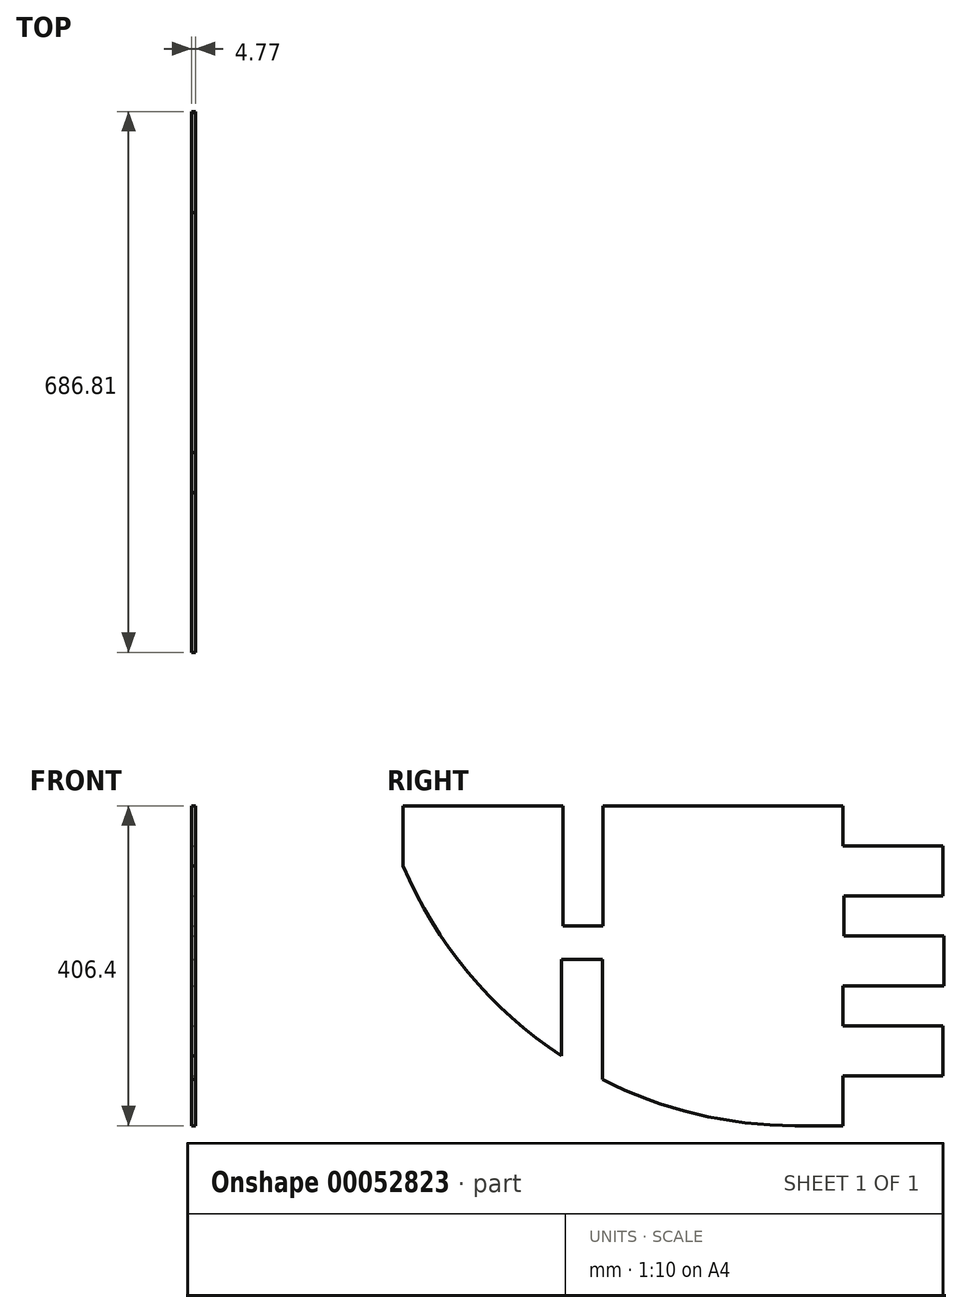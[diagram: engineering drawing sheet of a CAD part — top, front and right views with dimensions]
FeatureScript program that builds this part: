
annotation { "Feature Type Name" : "Feature", "Feature Type Description" : "" }
export const myFeature = defineFeature(function(context is Context, id is Id, definition is map)
    precondition{}
    {
        {
            var Q0;
            Q0=qCreatedBy(makeId("Front.planeOp"),FACE);
            var sketch = newSketch(context, id + "F0", { "sketchPlane" : qUnion([Q0])});
            skLineSegment(sketch, "E0", {"start": v(0, -406.4) * mm, "end": v(0, -342.9) * mm});
            skLineSegment(sketch, "E1", {"start": v(0, -50.8) * mm, "end": v(-127, -50.8) * mm});
            skLineSegment(sketch, "E2", {"start": v(-127, -50.8) * mm, "end": v(-127, -114.3) * mm});
            skLineSegment(sketch, "E3", {"start": v(-127, -114.3) * mm, "end": v(-1, -114.3) * mm});
            skLineSegment(sketch, "E4", {"start": v(-1, -165.1) * mm, "end": v(-128, -165.1) * mm});
            skLineSegment(sketch, "E5", {"start": v(-128, -165.1) * mm, "end": v(-128, -228.6) * mm});
            skLineSegment(sketch, "E6", {"start": v(-128, -228.6) * mm, "end": v(0, -228.6) * mm});
            skLineSegment(sketch, "E7", {"start": v(0, -279.4) * mm, "end": v(-127, -279.4) * mm});
            skLineSegment(sketch, "E8", {"start": v(-127, -279.4) * mm, "end": v(-127, -342.9) * mm});
            skLineSegment(sketch, "E9", {"start": v(-127, -342.9) * mm, "end": v(0, -342.9) * mm});
            skLineSegment(sketch, "E10.trimOffspring", {"start": v(0, -50.8) * mm, "end": v(0, 0) * mm});
            skLineSegment(sketch, "E11", {"start": v(0, 0) * mm, "end": v(304.8, 0) * mm});
            skLineSegment(sketch, "E12", {"start": v(558.8, 0) * mm, "end": v(558.8, -76.2) * mm});
            skLineSegment(sketch, "E13", {"start": v(0, -406.4) * mm, "end": v(60.96, -406.4) * mm});
            skArc(sketch, "E14", {"start": v(60.96, -406.4) * mm, "mid": v(186.87, -391.53) * mm, "end": v(305.85, -347.73) * mm});
            skPoint(sketch, "E15.start.orphan", {"position": v(-558.8, 0) * mm});
            skLineSegment(sketch, "E16", {"start": v(-1, -114.3) * mm, "end": v(-1, -165.1) * mm});
            skLineSegment(sketch, "E17", {"start": v(0, -228.6) * mm, "end": v(0, -279.4) * mm});
            skLineSegment(sketch, "E18", {"start": v(304.8, 0) * mm, "end": v(304.8, -152.4) * mm});
            skLineSegment(sketch, "E19", {"start": v(304.8, -152.4) * mm, "end": v(355.6, -152.4) * mm});
            skLineSegment(sketch, "E20", {"start": v(355.6, -152.4) * mm, "end": v(355.6, 0) * mm});
            skLineSegment(sketch, "E21.trimOffspring", {"start": v(355.6, 0) * mm, "end": v(558.8, 0) * mm});
            skLineSegment(sketch, "E22", {"start": v(305.85, -347.73) * mm, "end": v(305.85, -195.33) * mm});
            skLineSegment(sketch, "E23", {"start": v(305.85, -195.33) * mm, "end": v(357.41, -195.33) * mm});
            skLineSegment(sketch, "E24", {"start": v(357.41, -195.33) * mm, "end": v(357.41, -317.83) * mm});
            skArc(sketch, "E25.trimOffspring", {"start": v(357.41, -317.83) * mm, "mid": v(476.08, -211.99) * mm, "end": v(558.8, -76.2) * mm});
            skSolve(sketch);
        }
        {
            var Q0;
            Q0=makeQuery(id+"F0.imprint","IMPRINT",FACE,{"disambiguationData":[TD([[makeQuery(id+"F0.imprint","IMPRINT",EDGE,{"derivedFrom":sQuery(id+"F0.wireOp",EDGE,"E0")}),-1.0]])]});
            extrude(context, id + "F1", {"entities" : qUnion([Q0]), "depth" : 4.76 * mm});
        }
        {
            var Q0;
            Q0=makeQuery(id+"F1.opExtrude","SWEPT_BODY",BODY,{"disambiguationData":[OSD([sQuery(id+"F0.wireOp",EDGE,"E0"),sQuery(id+"F0.wireOp",EDGE,"E1"),sQuery(id+"F0.wireOp",EDGE,"E2"),sQuery(id+"F0.wireOp",EDGE,"E3"),sQuery(id+"F0.wireOp",EDGE,"E4"),sQuery(id+"F0.wireOp",EDGE,"E5"),sQuery(id+"F0.wireOp",EDGE,"E6"),sQuery(id+"F0.wireOp",EDGE,"E7"),sQuery(id+"F0.wireOp",EDGE,"E8"),sQuery(id+"F0.wireOp",EDGE,"E9"),sQuery(id+"F0.wireOp",EDGE,"E10.trimOffspring"),sQuery(id+"F0.wireOp",EDGE,"E11"),sQuery(id+"F0.wireOp",EDGE,"E12"),sQuery(id+"F0.wireOp",EDGE,"E13"),sQuery(id+"F0.wireOp",EDGE,"E14"),sQuery(id+"F0.wireOp",EDGE,"E16"),sQuery(id+"F0.wireOp",EDGE,"E17"),sQuery(id+"F0.wireOp",EDGE,"E18"),sQuery(id+"F0.wireOp",EDGE,"E19"),sQuery(id+"F0.wireOp",EDGE,"E20"),sQuery(id+"F0.wireOp",EDGE,"E21.trimOffspring"),sQuery(id+"F0.wireOp",EDGE,"E22"),sQuery(id+"F0.wireOp",EDGE,"E23"),sQuery(id+"F0.wireOp",EDGE,"E24"),sQuery(id+"F0.wireOp",EDGE,"E25.trimOffspring")])]});
            var Q1;
            Q1=makeQuery(id+"F1.opExtrude","CAP_EDGE",EDGE,{"disambiguationData":[OSD([sQuery(id+"F0.wireOp",EDGE,"E5")])],"isStart":false});
            transform(context, id + "F2", {"entities" : qUnion([Q0]), "transformType" : TransformType.ROTATION, "transformAxis" : qUnion([Q1]), "angle" : 90 * degree, "makeCopy" : false});
        }
    });
